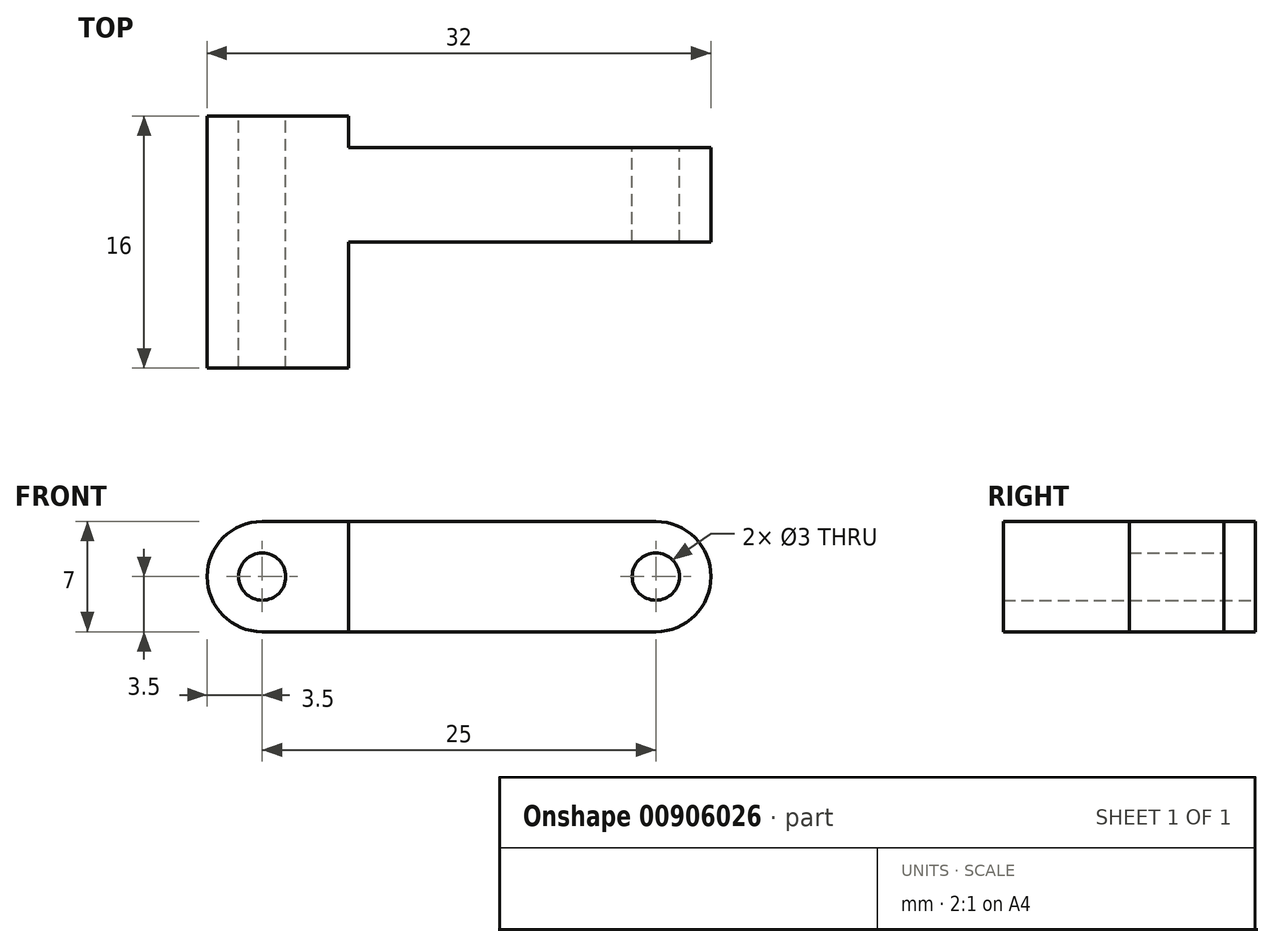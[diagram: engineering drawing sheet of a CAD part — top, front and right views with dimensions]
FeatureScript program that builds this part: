
annotation { "Feature Type Name" : "Feature", "Feature Type Description" : "" }
export const myFeature = defineFeature(function(context is Context, id is Id, definition is map)
    precondition{}
    {
        {
            var Q0;
            Q0=qCreatedBy(makeId("Front.planeOp"),FACE);
            var sketch = newSketch(context, id + "F0", { "sketchPlane" : qUnion([Q0])});
            skLineSegment(sketch, "E0", {"start": v(-12.5, 0) * mm, "end": v(12.5, 0) * mm});
            skArc(sketch, "E1", {"start": v(-12.5, 3.5) * mm, "mid": v(-16, 0) * mm, "end": v(-12.5, -3.5) * mm});
            skArc(sketch, "E2", {"start": v(12.5, -3.5) * mm, "mid": v(16, 0) * mm, "end": v(12.5, 3.5) * mm});
            skLineSegment(sketch, "E3", {"start": v(12.5, 3.5) * mm, "end": v(-12.5, 3.5) * mm});
            skLineSegment(sketch, "E4", {"start": v(-12.5, -3.5) * mm, "end": v(12.5, -3.5) * mm});
            skCircle(sketch, "E5", {"center": v(-12.5, 0) * mm, "radius": 1.5 * mm});
            skCircle(sketch, "E6", {"center": v(12.5, 0) * mm, "radius": 1.5 * mm});
            skSolve(sketch);
        }
        {
            var Q0;
            Q0=qSketchRegion(id+"F0",true);
            extrude(context, id + "F1", {"entities" : qUnion([Q0]), "endBound" : BoundingType.SYMMETRIC, "depth" : 16 * mm, "offsetDistance" : 25.4 * mm});
        }
        {
            var Q0;
            Q0=makeQuery(id+"F1.opExtrude","SWEPT_FACE",FACE,{"disambiguationData":[OSD([sQuery(id+"F0.wireOp",EDGE,"E3")])]});
            var sketch = newSketch(context, id + "F2", { "sketchPlane" : qUnion([Q0])});
            skLineSegment(sketch, "E7.bottom", {"start": v(33.74, 21.66) * mm, "end": v(-7, 21.66) * mm});
            skLineSegment(sketch, "E7.top", {"start": v(33.74, 6) * mm, "end": v(-7, 6) * mm});
            skLineSegment(sketch, "E7.left", {"start": v(33.74, 21.66) * mm, "end": v(33.74, 6) * mm});
            skLineSegment(sketch, "E7.right", {"start": v(-7, 21.66) * mm, "end": v(-7, 6) * mm});
            skLineSegment(sketch, "E8.bottom", {"start": v(38.29, -22.4) * mm, "end": v(-7, -22.4) * mm});
            skLineSegment(sketch, "E8.top", {"start": v(38.29, 0) * mm, "end": v(-7, 0) * mm});
            skLineSegment(sketch, "E8.left", {"start": v(38.29, -22.4) * mm, "end": v(38.29, 0) * mm});
            skLineSegment(sketch, "E8.right", {"start": v(-7, -22.4) * mm, "end": v(-7, 0) * mm});
            skSolve(sketch);
        }
        {
            var Q0;
            Q0=qSketchRegion(id+"F2",true);
            extrude(context, id + "F3", {"entities" : qUnion([Q0]), "operationType" : NewBodyOperationType.REMOVE, "oppositeDirection" : true, "depth" : 25.4 * mm, "offsetDistance" : 25.4 * mm});
        }
    });
